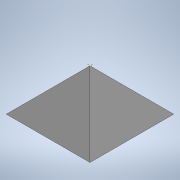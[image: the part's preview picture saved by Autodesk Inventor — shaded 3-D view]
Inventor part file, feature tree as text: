
AUTODESK INVENTOR PART (.ipt)
format: ipt  version: 2020 (Build 240168000, 168)  size: 127,488 bytes
history: native  units: in
note: dims shown in document units (in); Inventor stores cm internally (conversion verified against a paired STEP export)
features: sketch x6, extrude x5, plane x4
ambient origin geometry x8: Origin, YZ Plane, XZ Plane, XY Plane, X Axis, Y Axis, Z Axis, Center Point
bodies: Solid1 (feature_tree)
feature tree (15):
  extrude  "Extrusion1"  Depth=0.5906in
  sketch  "Sketch2"  dims[d2=0.2953in d3=0.0in]
  plane  "Work Plane1"
  plane  "Work Plane2"
  plane  "Work Plane3"
  plane  "Work Plane4"
  extrude  "Extrusion2"  TaperAngle=0.0deg  [1 undecoded]
  extrude  "Extrusion3"  Depth=0.1033in TaperAngle=0.0deg
  extrude  "Extrusion4"  TaperAngle=0.0deg  [1 undecoded]
  extrude  "Extrusion5"  [1 undecoded]
  sketch  "Sketch1"  dims[d0=0.5906in d1=0.5906in]
  sketch  "Sketch4"  dims[d4=0.1264in d5=0.0in d6=0.1033in d7=0.0in]
  sketch  "Sketch5"  dims[d8=0.5906in d9=0.0in]
  sketch  "Sketch6"  dims[d10=0.0508in d11=0.0in]
  sketch  "Sketch7"
note: 3 required parameter values undecoded (feature->parameter linkage not recoverable at this tier; creation-order binding heuristic only, values carry confidence <= 0.55)
